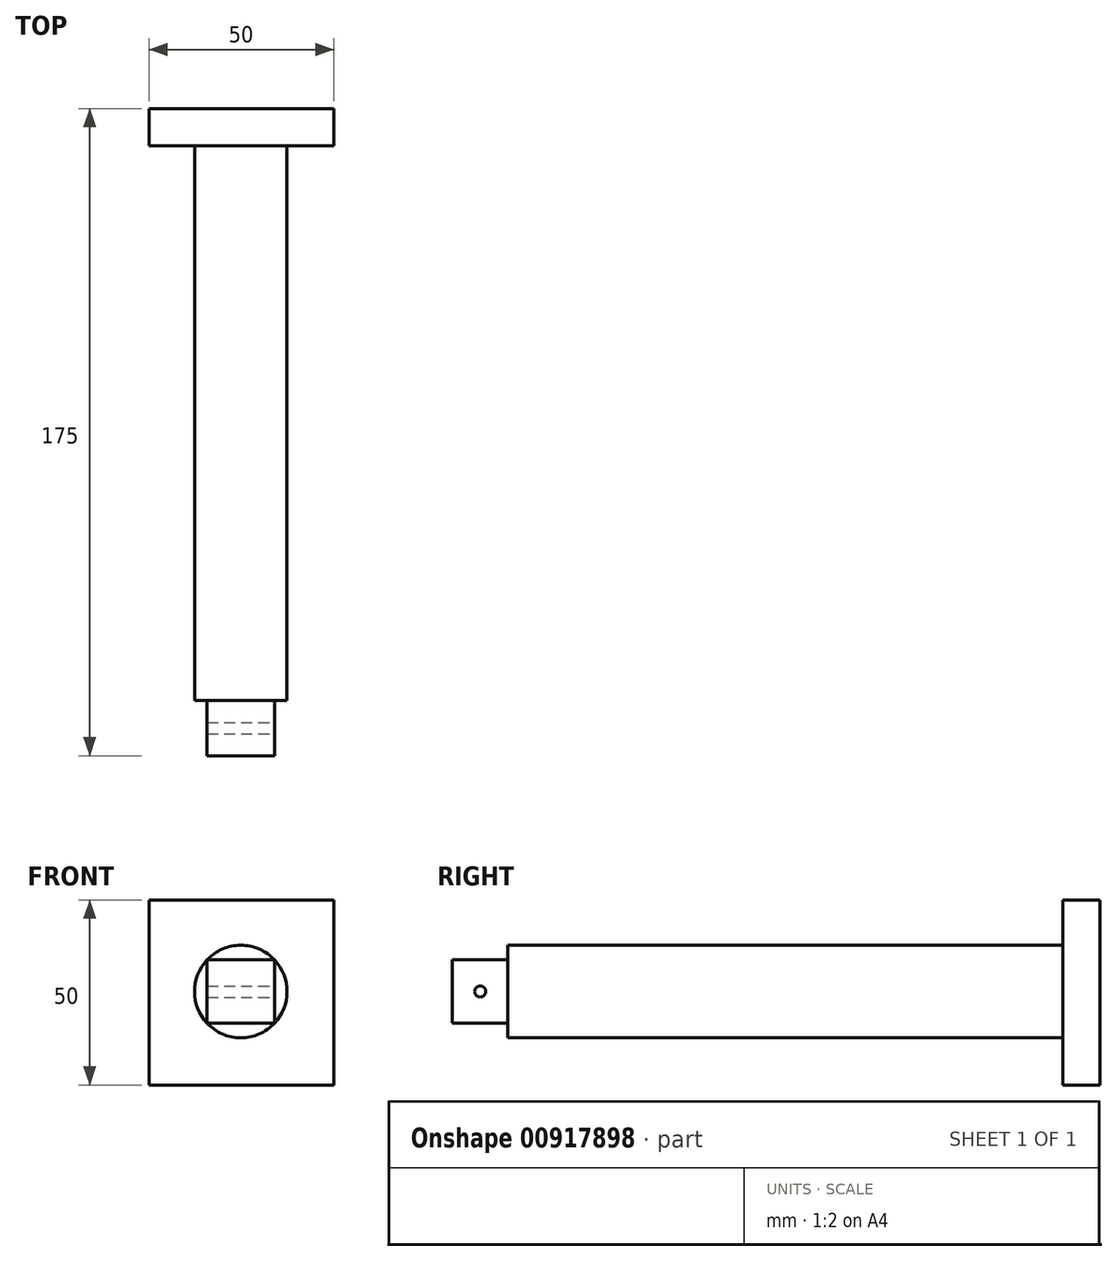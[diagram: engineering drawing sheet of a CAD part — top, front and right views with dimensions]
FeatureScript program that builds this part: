
annotation { "Feature Type Name" : "Feature", "Feature Type Description" : "" }
export const myFeature = defineFeature(function(context is Context, id is Id, definition is map)
    precondition{}
    {
        {
            var Q0;
            Q0=qCreatedBy(makeId("Front.planeOp"),FACE);
            var sketch = newSketch(context, id + "F0", { "sketchPlane" : qUnion([Q0])});
            skLineSegment(sketch, "E0.bottom", {"start": v(-59.28, 37.77) * mm, "end": v(-55.85, 37.77) * mm});
            skLineSegment(sketch, "E0.top", {"start": v(-59.28, 32.38) * mm, "end": v(-55.85, 32.38) * mm});
            skLineSegment(sketch, "E0.left", {"start": v(-59.28, 37.77) * mm, "end": v(-59.28, 32.38) * mm});
            skLineSegment(sketch, "E0.right", {"start": v(-55.85, 37.77) * mm, "end": v(-55.85, 32.38) * mm});
            skLineSegment(sketch, "E1.bottom", {"start": v(-7.87, -51.34) * mm, "end": v(-57.87, -51.34) * mm});
            skLineSegment(sketch, "E1.top", {"start": v(-7.87, -1.34) * mm, "end": v(-57.87, -1.34) * mm});
            skLineSegment(sketch, "E1.left", {"start": v(-7.87, -51.34) * mm, "end": v(-7.87, -1.34) * mm});
            skLineSegment(sketch, "E1.right", {"start": v(-57.87, -51.34) * mm, "end": v(-57.87, -1.34) * mm});
            skSolve(sketch);
        }
        {
            var Q0;
            Q0=makeQuery(id+"F0.imprint","IMPRINT",FACE,{"disambiguationData":[TD([[makeQuery(id+"F0.imprint","IMPRINT",EDGE,{"derivedFrom":sQuery(id+"F0.wireOp",EDGE,"E1.bottom")}),-1.0]])]});
            extrude(context, id + "F1", {"entities" : qUnion([Q0]), "depth" : 10 * mm, "offsetDistance" : 25 * mm});
        }
        {
            var Q0;
            Q0=makeQuery(id+"F1.opExtrude","CAP_FACE",FACE,{"disambiguationData":[OSD([sQuery(id+"F0.wireOp",EDGE,"E1.bottom"),sQuery(id+"F0.wireOp",EDGE,"E1.top"),sQuery(id+"F0.wireOp",EDGE,"E1.left"),sQuery(id+"F0.wireOp",EDGE,"E1.right")])],"isStart":false});
            var sketch = newSketch(context, id + "F2", { "sketchPlane" : qUnion([Q0])});
            skLineSegment(sketch, "E2", {"start": v(-57.87, -1.34) * mm, "end": v(-7.87, -51.34) * mm});
            skLineSegment(sketch, "E3", {"start": v(-7.87, -51.34) * mm, "end": v(-57.87, -51.34) * mm});
            skLineSegment(sketch, "E4", {"start": v(-57.87, -51.34) * mm, "end": v(-7.87, -1.34) * mm});
            skLineSegment(sketch, "E5", {"start": v(-7.87, -1.34) * mm, "end": v(-32.87, -26.34) * mm});
            skSolve(sketch);
        }
        {
            var Q0;
            {var subQ0=sQuery(id+"F2.wireOp",EDGE,"E3");Q0=makeQuery(id+"F2.imprint","IMPRINT",FACE,{"disambiguationData":[TD([[makeQuery(id+"F2.imprint","IMPRINT",EDGE,{"derivedFrom":subQ0}),-1.0]])]});}
            var sketch = newSketch(context, id + "F3", { "sketchPlane" : qUnion([Q0])});
            skCircle(sketch, "E6", {"center": v(-33.04, -26.08) * mm, "radius": 7.5 * mm});
            skCircle(sketch, "E7", {"center": v(-33.04, -26.08) * mm, "radius": 12.5 * mm});
            skSolve(sketch);
        }
        {
            var Q0;
            {var subQ2=sQuery(id+"F2.wireOp",EDGE,"E4");var subQ5=makeQuery(id+"F2.imprint","IMPRINT",EDGE,{"derivedFrom":subQ2});var subQ7=sQuery(id+"F3.wireOp",EDGE,"E7");var subQ9=makeQuery(id+"F3.imprint","INTERSECT",VERTEX,{"derivedFrom":[subQ5,subQ7]});Q0=makeQuery(id+"F3.imprint","IMPRINT",FACE,{"disambiguationData":[TD([[makeQuery(id+"F3.imprint","IMPRINT",EDGE,{"disambiguationData":[TD([[subQ9,-1.0]])],"derivedFrom":subQ5}),1.0]])]});}
            var Q1;
            {var subQ0=sQuery(id+"F3.wireOp",EDGE,"E6");var subQ2=sQuery(id+"F2.wireOp",EDGE,"E4");var subQ5=makeQuery(id+"F2.imprint","IMPRINT",EDGE,{"derivedFrom":subQ2});var subQ6=makeQuery(id+"F3.imprint","INTERSECT",VERTEX,{"derivedFrom":[subQ5,subQ0]});Q1=makeQuery(id+"F3.imprint","IMPRINT",FACE,{"disambiguationData":[TD([[makeQuery(id+"F3.imprint","IMPRINT",EDGE,{"disambiguationData":[TD([[subQ6,-1.0]])],"derivedFrom":subQ0}),1.0]])]});}
            var Q2;
            {var subQ0=sQuery(id+"F3.wireOp",EDGE,"E6");var subQ2=sQuery(id+"F2.wireOp",EDGE,"E4");var subQ5=makeQuery(id+"F2.imprint","IMPRINT",EDGE,{"derivedFrom":subQ2});var subQ6=makeQuery(id+"F3.imprint","INTERSECT",VERTEX,{"derivedFrom":[subQ5,subQ0]});Q2=makeQuery(id+"F3.imprint","IMPRINT",FACE,{"disambiguationData":[TD([[makeQuery(id+"F3.imprint","IMPRINT",EDGE,{"disambiguationData":[TD([[subQ6,1.0]])],"derivedFrom":subQ0}),1.0]])]});}
            var Q3;
            {var subQ2=sQuery(id+"F2.wireOp",EDGE,"E4");var subQ5=makeQuery(id+"F2.imprint","IMPRINT",EDGE,{"derivedFrom":subQ2});var subQ7=sQuery(id+"F3.wireOp",EDGE,"E7");var subQ8=makeQuery(id+"F3.imprint","INTERSECT",VERTEX,{"derivedFrom":[subQ5,subQ7]});Q3=makeQuery(id+"F3.imprint","IMPRINT",FACE,{"disambiguationData":[TD([[makeQuery(id+"F3.imprint","IMPRINT",EDGE,{"disambiguationData":[TD([[subQ8,-1.0]])],"derivedFrom":subQ5}),-1.0]])]});}
            extrude(context, id + "F4", {"entities" : qUnion([Q0, Q1, Q2, Q3]), "operationType" : NewBodyOperationType.ADD, "depth" : 150 * mm, "offsetDistance" : 25 * mm});
        }
        {
            var Q0;
            Q0=makeQuery(id+"F4.opExtrude","CAP_FACE",FACE,{"disambiguationData":[OSD([sQuery(id+"F3.wireOp",EDGE,"E7")])],"isStart":false});
            var sketch = newSketch(context, id + "F5", { "sketchPlane" : qUnion([Q0])});
            skLineSegment(sketch, "E8.bottom", {"start": v(-23.94, -34.64) * mm, "end": v(-42.15, -34.64) * mm});
            skLineSegment(sketch, "E8.top", {"start": v(-23.94, -17.52) * mm, "end": v(-42.15, -17.52) * mm});
            skLineSegment(sketch, "E8.left", {"start": v(-23.94, -34.64) * mm, "end": v(-23.94, -17.52) * mm});
            skLineSegment(sketch, "E8.right", {"start": v(-42.15, -34.64) * mm, "end": v(-42.15, -17.52) * mm});
            skPoint(sketch, "E8.middle", {"position": v(-33.04, -26.08) * mm});
            skSolve(sketch);
        }
        {
            var Q0;
            Q0=makeQuery(id+"F5.imprint","IMPRINT",FACE,{"disambiguationData":[TD([[makeQuery(id+"F5.imprint","IMPRINT",EDGE,{"derivedFrom":sQuery(id+"F5.wireOp",EDGE,"E8.bottom")}),-1.0]])]});
            extrude(context, id + "F6", {"entities" : qUnion([Q0]), "operationType" : NewBodyOperationType.ADD, "depth" : 15 * mm, "offsetDistance" : 25 * mm});
        }
        {
            var Q0;
            Q0=makeQuery(id+"F6.opExtrude","SWEPT_FACE",FACE,{"disambiguationData":[OSD([sQuery(id+"F5.wireOp",EDGE,"E8.left")])]});
            var sketch = newSketch(context, id + "F7", { "sketchPlane" : qUnion([Q0])});
            skLineSegment(sketch, "E9", {"start": v(-167.5, -17.52) * mm, "end": v(-167.5, -33.77) * mm});
            skLineSegment(sketch, "E10", {"start": v(-167.5, -33.77) * mm, "end": v(-175, -26.08) * mm});
            skLineSegment(sketch, "E11", {"start": v(-175, -26.08) * mm, "end": v(-167.5, -26.08) * mm});
            skLineSegment(sketch, "E12", {"start": v(-167.5, -26.08) * mm, "end": v(-175, -26.08) * mm});
            skSolve(sketch);
        }
        {
            var Q0;
            Q0=sQuery(id+"F7.wireOp",VERTEX,"E11.end");
            var Q1;
            Q1=makeQuery(id+"F1.opExtrude","SWEPT_BODY",BODY,{"disambiguationData":[OSD([sQuery(id+"F0.wireOp",EDGE,"E1.bottom"),sQuery(id+"F0.wireOp",EDGE,"E1.top"),sQuery(id+"F0.wireOp",EDGE,"E1.left"),sQuery(id+"F0.wireOp",EDGE,"E1.right")])]});
            hole(context, id + "F8", {"style" : HoleStyle.SIMPLE, "endStyle" : HoleEndStyle.BLIND, "holeDiameter" : 3 * mm, "majorDiameter" : 5 * mm, "holeDepth" : 50 * mm, "isTappedThrough" : true, "tappedDepth" : 12 * mm, "tapClearance" : 3, "locations" : qUnion([Q0]), "scope" : qUnion([Q1])});
        }
    });
